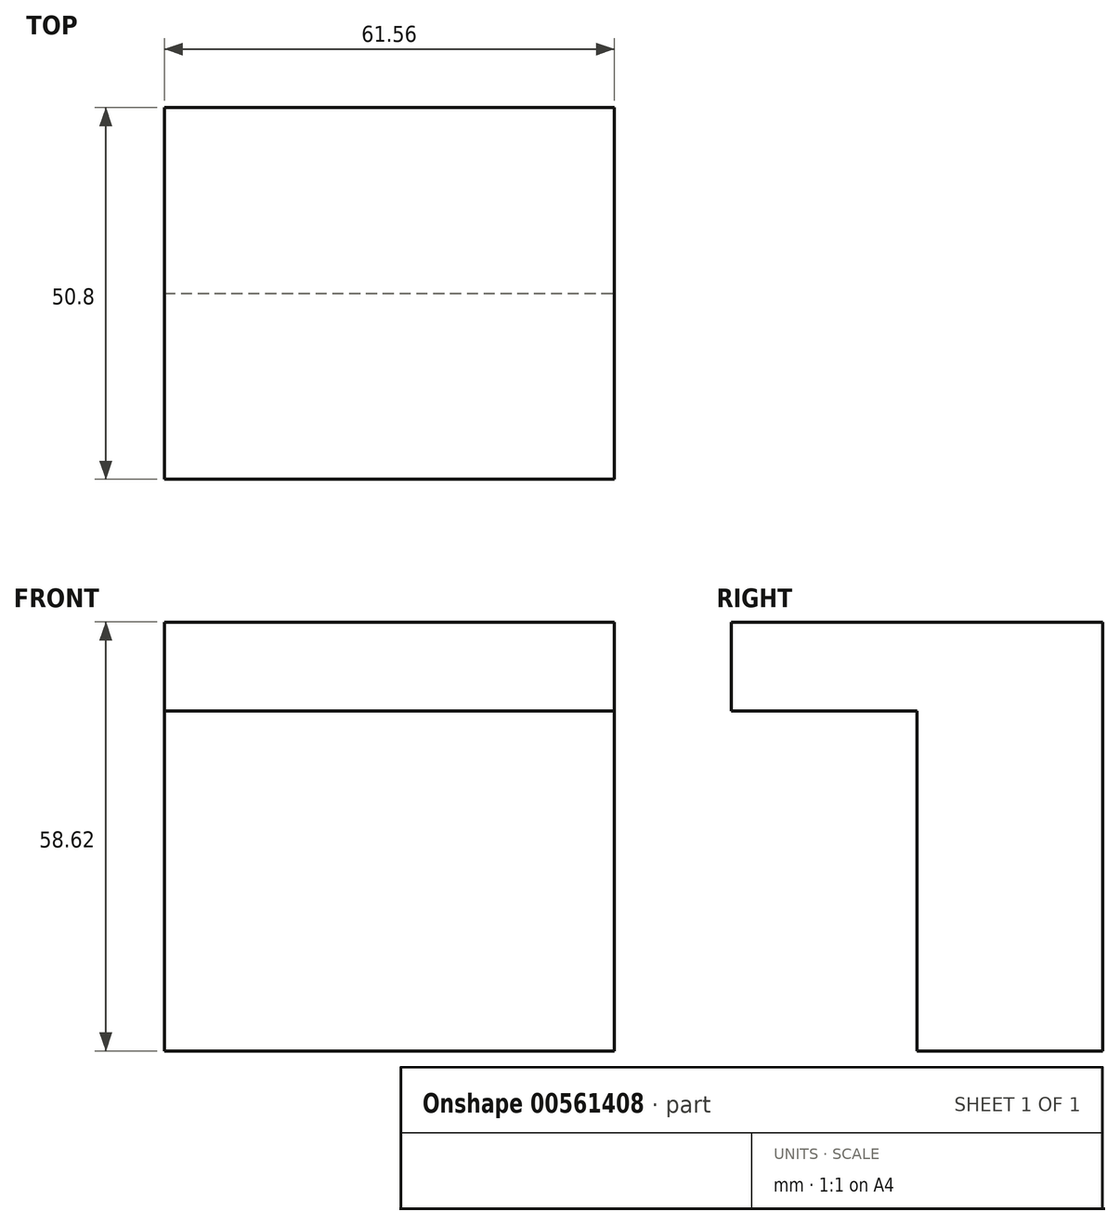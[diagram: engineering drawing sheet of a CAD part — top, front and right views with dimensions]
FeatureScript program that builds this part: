
annotation { "Feature Type Name" : "Feature", "Feature Type Description" : "" }
export const myFeature = defineFeature(function(context is Context, id is Id, definition is map)
    precondition{}
    {
        {
            var Q0;
            Q0=qCreatedBy(makeId("Front.planeOp"),FACE);
            cPlane(context, id + "F0", {"entities" : qUnion([Q0]), "cplaneType" : CPlaneType.OFFSET, "offset" : 25.4 * mm, "width" : 152.4 * mm, "height" : 152.4 * mm});
        }
        {
            var Q0;
            Q0=qCreatedBy(id+"F0.planeOp",FACE);
            var sketch = newSketch(context, id + "F1", { "sketchPlane" : qUnion([Q0])});
            skLineSegment(sketch, "E0.bottom", {"start": v(15.13, 17.24) * mm, "end": v(76.69, 17.24) * mm});
            skLineSegment(sketch, "E0.top", {"start": v(15.13, 75.86) * mm, "end": v(76.69, 75.86) * mm});
            skLineSegment(sketch, "E0.left", {"start": v(15.13, 17.24) * mm, "end": v(15.13, 75.86) * mm});
            skLineSegment(sketch, "E0.right", {"start": v(76.69, 17.24) * mm, "end": v(76.69, 75.86) * mm});
            skSolve(sketch);
        }
        {
            var Q0;
            Q0 = qSketchRegion(id + "F1", true);
            extrude(context, id + "F2", {"entities" : qUnion([Q0]), "depth" : 25.4 * mm, "offsetDistance" : 25.4 * mm});
        }
        {
            var Q0;
            Q0=makeQuery(id+"F2.opExtrude","CAP_FACE",FACE,{"disambiguationData":[OSD([sQuery(id+"F1.wireOp",EDGE,"E0.bottom"),sQuery(id+"F1.wireOp",EDGE,"E0.top"),sQuery(id+"F1.wireOp",EDGE,"E0.left"),sQuery(id+"F1.wireOp",EDGE,"E0.right")])],"isStart":false});
            var sketch = newSketch(context, id + "F3", { "sketchPlane" : qUnion([Q0])});
            skLineSegment(sketch, "E1.bottom", {"start": v(15.13, 75.86) * mm, "end": v(76.69, 75.86) * mm});
            skLineSegment(sketch, "E1.top", {"start": v(15.13, 63.69) * mm, "end": v(76.69, 63.69) * mm});
            skLineSegment(sketch, "E1.left", {"start": v(15.13, 75.86) * mm, "end": v(15.13, 63.69) * mm});
            skLineSegment(sketch, "E1.right", {"start": v(76.69, 75.86) * mm, "end": v(76.69, 63.69) * mm});
            skSolve(sketch);
        }
        {
            var Q0;
            Q0=makeQuery(id+"F3.imprint","IMPRINT",FACE,{"disambiguationData":[TD([[makeQuery(id+"F3.imprint","IMPRINT",EDGE,{"derivedFrom":sQuery(id+"F3.wireOp",EDGE,"E1.bottom")}),-1.0]])]});
            extrude(context, id + "F4", {"entities" : qUnion([Q0]), "operationType" : NewBodyOperationType.ADD, "depth" : 25.4 * mm, "offsetDistance" : 25.4 * mm});
        }
    });
